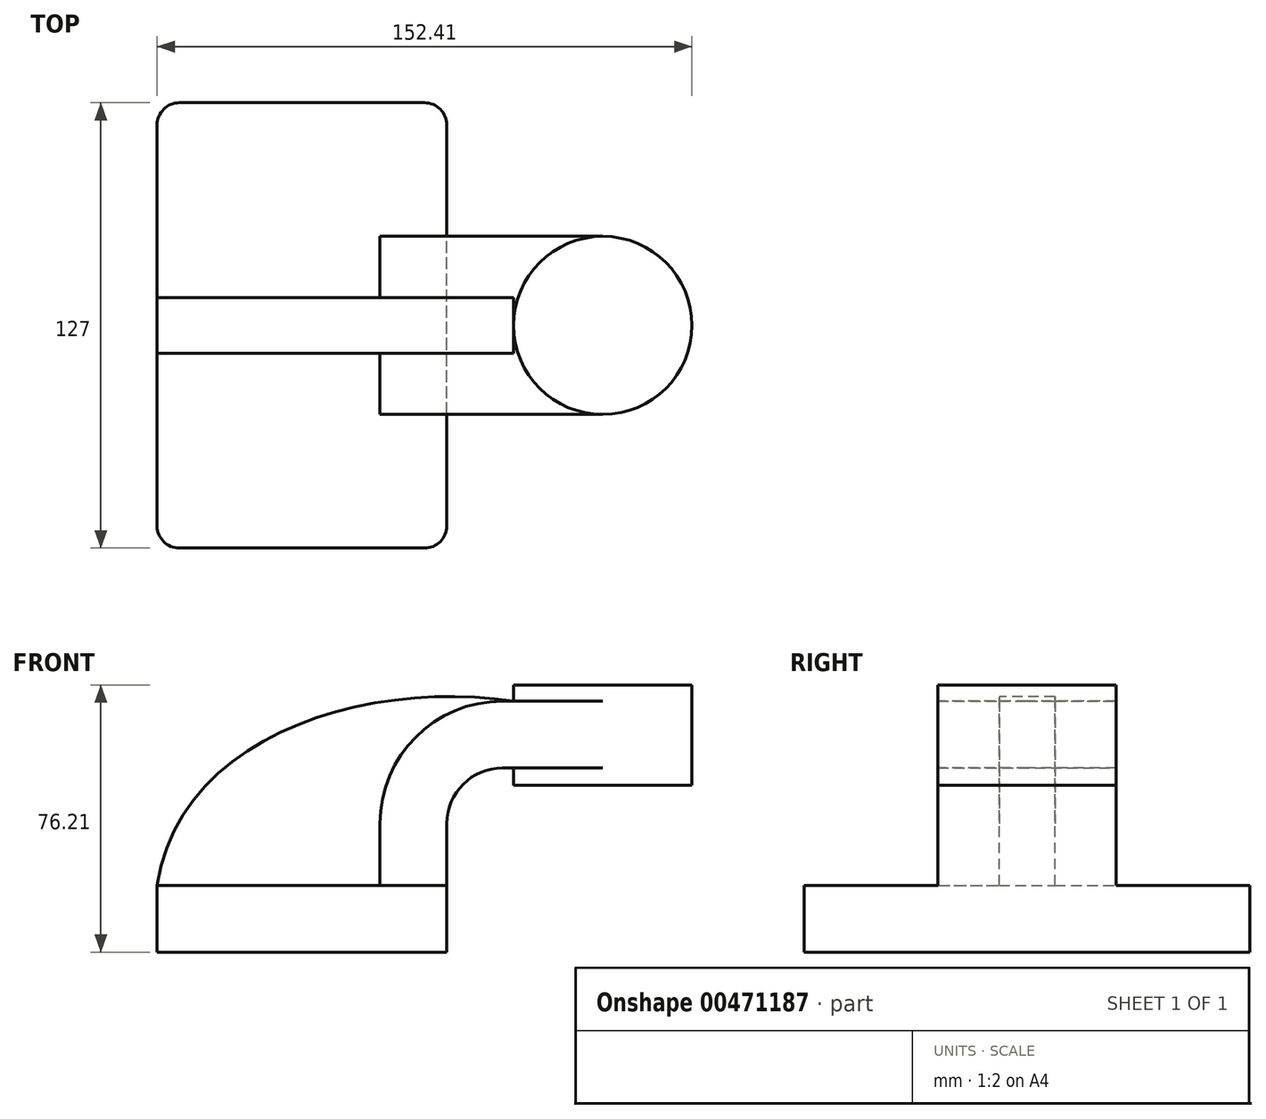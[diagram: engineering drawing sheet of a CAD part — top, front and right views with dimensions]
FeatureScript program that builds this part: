
annotation { "Feature Type Name" : "Feature", "Feature Type Description" : "" }
export const myFeature = defineFeature(function(context is Context, id is Id, definition is map)
    precondition{}
    {
        {
            var Q0;
            Q0=qCreatedBy(makeId("Front.planeOp"),FACE);
            var sketch = newSketch(context, id + "F0", { "sketchPlane" : qUnion([Q0])});
            skLineSegment(sketch, "E0.bottom", {"start": v(41.28, -9.52) * mm, "end": v(-41.28, -9.52) * mm});
            skLineSegment(sketch, "E0.top", {"start": v(41.28, 9.53) * mm, "end": v(-41.28, 9.53) * mm});
            skLineSegment(sketch, "E0.left", {"start": v(41.28, -9.52) * mm, "end": v(41.28, 9.53) * mm});
            skLineSegment(sketch, "E0.right", {"start": v(-41.28, -9.52) * mm, "end": v(-41.28, 9.53) * mm});
            skPoint(sketch, "E0.middle", {"position": v(0, 0) * mm});
            skLineSegment(sketch, "E1", {"start": v(41.28, 9.53) * mm, "end": v(41.28, 27.1) * mm});
            skLineSegment(sketch, "E2.bottom", {"start": v(111.12, 38.1) * mm, "end": v(60.32, 38.1) * mm});
            skLineSegment(sketch, "E2.top", {"start": v(111.12, 66.68) * mm, "end": v(60.32, 66.68) * mm});
            skLineSegment(sketch, "E2.left", {"start": v(111.12, 38.1) * mm, "end": v(111.12, 66.68) * mm});
            skLineSegment(sketch, "E2.right", {"start": v(60.32, 38.1) * mm, "end": v(60.32, 66.68) * mm});
            skPoint(sketch, "E2.middle", {"position": v(85.72, 52.39) * mm});
            skArc(sketch, "E3", {"start": v(57.15, 42.98) * mm, "mid": v(45.92, 38.33) * mm, "end": v(41.27, 27.1) * mm});
            skLineSegment(sketch, "E4", {"start": v(57.15, 42.98) * mm, "end": v(85.72, 42.98) * mm});
            skLineSegment(sketch, "E5.0", {"start": v(22.23, 9.53) * mm, "end": v(22.23, 27.1) * mm});
            skArc(sketch, "E5.1", {"start": v(57.15, 62.03) * mm, "mid": v(32.45, 51.8) * mm, "end": v(22.23, 27.1) * mm});
            skLineSegment(sketch, "E5.2", {"start": v(57.15, 62.03) * mm, "end": v(85.72, 62.03) * mm});
            skLineSegment(sketch, "E6", {"start": v(85.72, 38.1) * mm, "end": v(85.72, 66.68) * mm});
            skFitSpline(sketch, "E7", {"points": [v(-41.28, 9.52) * mm, v(60.32, 62.03) * mm], "startDerivative": vector(19.67, 129.5) * mm, "endDerivative": vector(124.78, -18.63) * mm});
            skSolve(sketch);
        }
        {
            var Q0;
            Q0=makeQuery(id+"F0.imprint","IMPRINT",FACE,{"disambiguationData":[TD([[makeQuery(id+"F0.imprint","IMPRINT",EDGE,{"derivedFrom":sQuery(id+"F0.wireOp",EDGE,"E0.bottom")}),-1.0]])]});
            extrude(context, id + "F1", {"entities" : qUnion([Q0]), "endBound" : BoundingType.SYMMETRIC, "depth" : 127 * mm});
        }
        {
            var Q0;
            {var subQ6=sQuery(id+"F0.wireOp",EDGE,"E1");Q0=makeQuery(id+"F0.imprint","IMPRINT",FACE,{"disambiguationData":[TD([[makeQuery(id+"F0.imprint","IMPRINT",EDGE,{"derivedFrom":subQ6}),1.0]])]});}
            var Q1;
            {var subQ3=sQuery(id+"F0.wireOp",EDGE,"E4");var subQ5=sQuery(id+"F0.wireOp",EDGE,"E6");var subQ6=makeQuery(id+"F0.imprint","INTERSECT",VERTEX,{"derivedFrom":[subQ3,subQ5]});Q1=makeQuery(id+"F0.imprint","IMPRINT",FACE,{"disambiguationData":[TD([[makeQuery(id+"F0.imprint","IMPRINT",EDGE,{"disambiguationData":[TD([[subQ6,1.0]])],"derivedFrom":subQ3}),1.0]])]});}
            extrude(context, id + "F2", {"entities" : qUnion([Q0, Q1]), "operationType" : NewBodyOperationType.ADD, "endBound" : BoundingType.SYMMETRIC, "depth" : 50.8 * mm});
        }
        {
            var Q0;
            {var subQ3=sQuery(id+"F0.wireOp",EDGE,"E5.0");Q0=makeQuery(id+"F0.imprint","IMPRINT",FACE,{"disambiguationData":[TD([[makeQuery(id+"F0.imprint","IMPRINT",EDGE,{"derivedFrom":subQ3}),1.0]])]});}
            extrude(context, id + "F3", {"entities" : qUnion([Q0]), "operationType" : NewBodyOperationType.ADD, "endBound" : BoundingType.SYMMETRIC, "depth" : 15.88 * mm});
        }
        {
            var Q0;
            {var subQ0=sQuery(id+"F0.wireOp",EDGE,"E2.left");Q0=makeQuery(id+"F0.imprint","IMPRINT",FACE,{"disambiguationData":[TD([[makeQuery(id+"F0.imprint","IMPRINT",EDGE,{"derivedFrom":subQ0}),1.0]])]});}
            var Q1;
            Q1=sQuery(id+"F0.wireOp",EDGE,"E6");
            revolve(context, id + "F4", {"operationType" : NewBodyOperationType.ADD, "entities" : qUnion([Q0]), "axis" : qUnion([Q1]), "revolveType" : RevolveType.FULL});
        }
        {
            var Q0;
            Q0=makeQuery(id+"F1.opExtrude","CAP_EDGE",EDGE,{"disambiguationData":[OSD([sQuery(id+"F0.wireOp",EDGE,"E0.left")])],"isStart":false});
            var Q1;
            Q1=makeQuery(id+"F1.opExtrude","CAP_EDGE",EDGE,{"disambiguationData":[OSD([sQuery(id+"F0.wireOp",EDGE,"E0.left")])],"isStart":true});
            var Q2;
            Q2=makeQuery(id+"F1.opExtrude","CAP_EDGE",EDGE,{"disambiguationData":[OSD([sQuery(id+"F0.wireOp",EDGE,"E0.right")])],"isStart":false});
            var Q3;
            Q3=makeQuery(id+"F1.opExtrude","CAP_EDGE",EDGE,{"disambiguationData":[OSD([sQuery(id+"F0.wireOp",EDGE,"E0.right")])],"isStart":true});
            fillet(context, id + "F5", {"entities" : qUnion([Q0, Q1, Q2, Q3]), "radius" : 6.35 * mm, "tangentPropagation" : true, "allowEdgeOverflow" : false});
        }
    });
